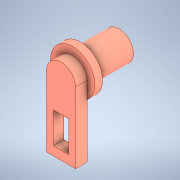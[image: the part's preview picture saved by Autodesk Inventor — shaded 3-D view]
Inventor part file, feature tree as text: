
AUTODESK INVENTOR PART (.ipt)
format: ipt  version: 2020.1 (Build 241239000, 239)  size: 248,320 bytes
history: native  units: in
note: dims shown in document units (in); Inventor stores cm internally (conversion verified against a paired STEP export)
features: extrude x5, sketch x5, projected_geometry x3, plane x2, other x1, fillet x1, split x1
ambient origin geometry x8: Origin, YZ Plane, XZ Plane, XY Plane, X Axis, Y Axis, Z Axis, Center Point
bodies: Solid1 (feature_tree)
feature tree (18):
  parser-record x1  (decoder bookkeeping rows leaked as tree rows — omitted from the tree; the rows remain in map.json)
  extrude  "Extrusion1"  Depth=0.0787in
  extrude  "Extrusion2"  Depth=0.2953in
  plane  "Work Plane2"
  extrude  "Extrusion7"  TaperAngle=0.0deg  [1 undecoded]
  extrude  "Extrusion8"  Depth=0.0787in
  extrude  "Extrusion9"  TaperAngle=0.0deg  [1 undecoded]
  fillet  "Fillet2"  Radius=0.7218in
  plane  "Work Plane3"
  split  "Split1"
  sketch  "Sketch1"  dims[d0=0.7874in d1=0.0787in]
  sketch  "Sketch2"  dims[d2=0.0in d3=0.2953in]
  sketch  "Sketch7"  dims[d4=0.5906in d5=0.0in]
  projected_geometry  "Projected Loop3"
  sketch  "Sketch8"  dims[d26=-0.3937in d27=0.0787in]
  projected_geometry  "Projected Loop4"
  sketch  "Sketch9"  dims[d28=0.0787in d29=0.0in d31=0.7218in d32=0.1181in d33=0.0in d34=0.0787in d35=0.1575in d36=0.315in d37=0.315in d38=0.3937in d39=0.0137in d40=0.0098in d41=0.0in]
  projected_geometry  "Projected Loop5"
note: 2 required parameter values undecoded (feature->parameter linkage not recoverable at this tier; creation-order binding heuristic only, values carry confidence <= 0.55)
note: 1 file-system path scrubbed to <path> (originals preserved in map.json)
